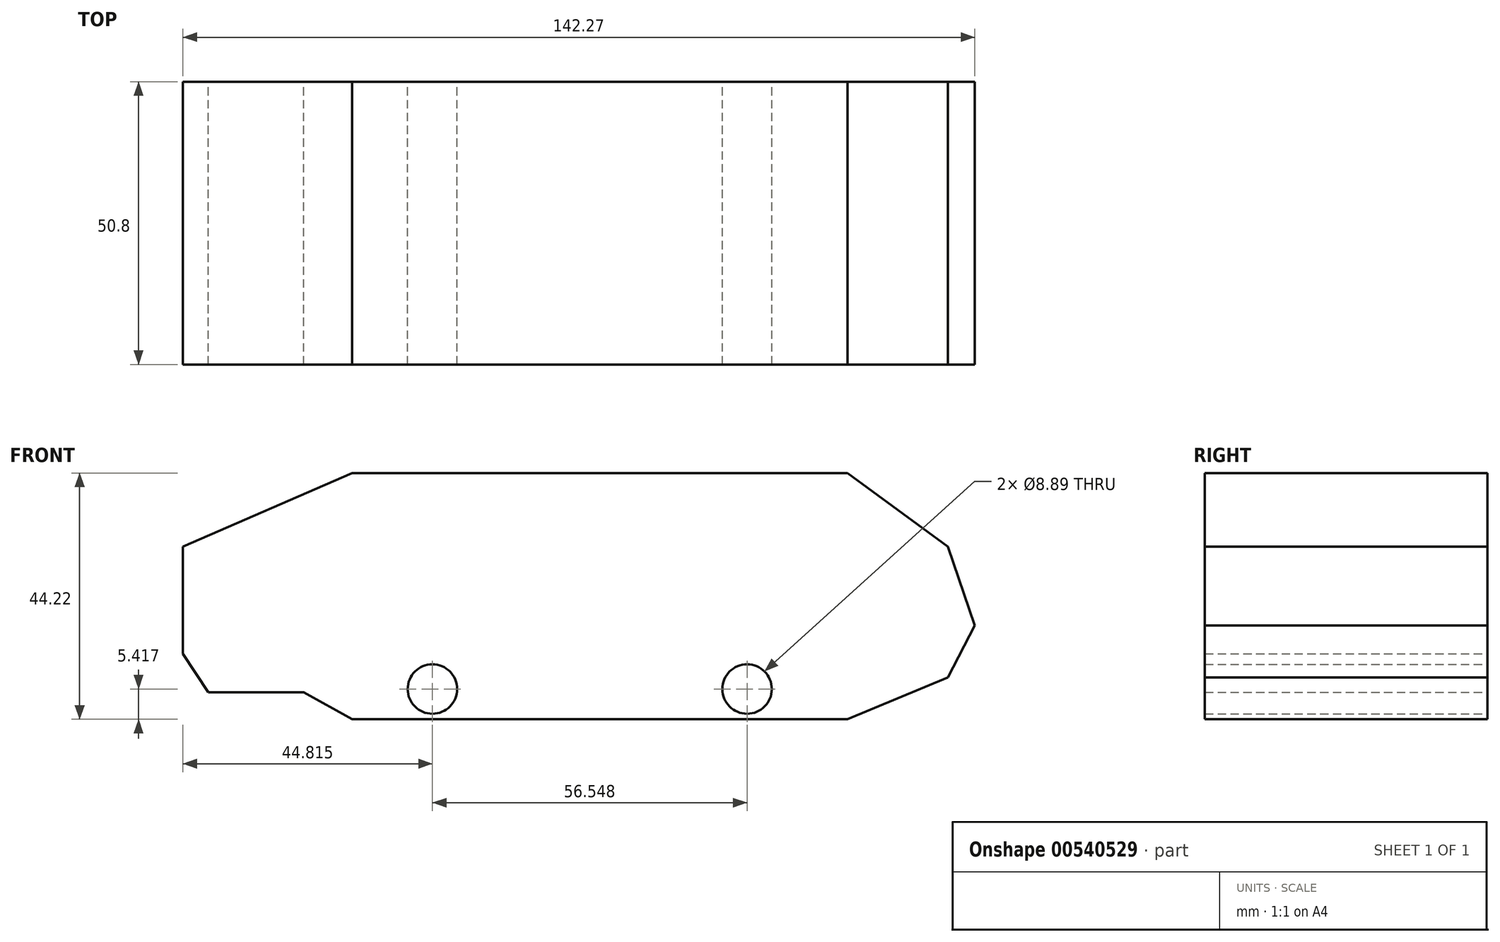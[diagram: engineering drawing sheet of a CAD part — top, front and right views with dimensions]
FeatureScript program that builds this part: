
annotation { "Feature Type Name" : "Feature", "Feature Type Description" : "" }
export const myFeature = defineFeature(function(context is Context, id is Id, definition is map)
    precondition{}
    {
        {
            var Q0;
            Q0=qCreatedBy(makeId("Front.planeOp"),FACE);
            var sketch = newSketch(context, id + "F0", { "sketchPlane" : qUnion([Q0])});
            skLineSegment(sketch, "E0", {"start": v(-35.2, 18.65) * mm, "end": v(53.84, 18.65) * mm});
            skLineSegment(sketch, "E1", {"start": v(53.84, 18.65) * mm, "end": v(71.89, 5.41) * mm});
            skLineSegment(sketch, "E2", {"start": v(71.89, 5.41) * mm, "end": v(76.7, -8.72) * mm});
            skLineSegment(sketch, "E3", {"start": v(76.7, -8.72) * mm, "end": v(71.89, -18.05) * mm});
            skLineSegment(sketch, "E4", {"start": v(71.89, -18.05) * mm, "end": v(53.84, -25.57) * mm});
            skLineSegment(sketch, "E5", {"start": v(53.84, -25.57) * mm, "end": v(-35.2, -25.57) * mm});
            skLineSegment(sketch, "E6", {"start": v(-35.2, -25.57) * mm, "end": v(-43.92, -20.75) * mm});
            skLineSegment(sketch, "E7", {"start": v(-43.92, -20.75) * mm, "end": v(-61.06, -20.75) * mm});
            skLineSegment(sketch, "E8", {"start": v(-61.06, -20.75) * mm, "end": v(-65.57, -13.84) * mm});
            skLineSegment(sketch, "E9", {"start": v(-65.57, -13.84) * mm, "end": v(-65.57, 5.41) * mm});
            skLineSegment(sketch, "E10", {"start": v(-65.57, 5.41) * mm, "end": v(-35.2, 18.65) * mm});
            skCircle(sketch, "E11", {"center": v(-20.75, -20.15) * mm, "radius": 4.45 * mm});
            skCircle(sketch, "E12", {"center": v(35.8, -20.15) * mm, "radius": 4.45 * mm});
            skSolve(sketch);
        }
        {
            var Q0;
            Q0=makeQuery(id+"F0.imprint","IMPRINT",FACE,{"disambiguationData":[TD([[makeQuery(id+"F0.imprint","IMPRINT",EDGE,{"derivedFrom":sQuery(id+"F0.wireOp",EDGE,"E0")}),-1.0]])]});
            extrude(context, id + "F1", {"entities" : qUnion([Q0]), "depth" : 50.8 * mm, "offsetDistance" : 25.4 * mm});
        }
    });
